# Revit family: Indoor_Floor Lamp_Santa&Cole_Diana-Diana Mayor
name_source: partatom
category: Luminarias
revit_build: Autodesk Revit 2018 (Build: 20190510_1515(x64)
units: mm (PartAtom-declared; Revit-internal decimal feet)

## family parameters
Compartido = No
Corte con vacíos al cargar = No
Cota de conector redondo = Diámetro de uso
Número OmniClass = 23.80.70.00
Origen de luz = Sí
Punto de cálculo de habitación = No
Se basa en plano de trabajo = No
Siempre vertical = Sí
Tipo de pieza = Normal
Título OmniClass = Lighting

## types (8) — shared parameters
Assembly instructions - CE = https://www.santacole.com
Assembly instructions - UL = https://www.santacole.com
Cambio de temperatura de color de luz atenuada = <Ninguno>
Carga aparente = 12 VA
Energy Label = https://www.santacole.com
Fabricante = Santa & Cole
Filtro de color = 16777215
Load = 12 W
Manufacturer website = http://www.santacole.com
Modelo = Diana
Second Bulb = Bulb : 1521 lm
Tamaño de símbolo de origen de luz = 50 mm  [stored 0.164042 ft]
Technical Information = https://www.santacole.com
URL = https://www.santacole.com

## per-type parameters (varying)
| type | Code | Lampshade Material | Light Source Elevation | Structure Material | Visibility_Diana | Visibility_Diana Mayor |
| Diana - Black Linen Lampshade with Brass Structure | DIA31/DIA313+DIAGx | Santa & Cole - Black Linen | 1264 mm | Santa & Cole - Brass | Sí | No |
| Diana - Black Linen Lampshade with Nickel Structure | DIA21/DIA213+DIAMx | Santa & Cole - Black Linen | 1264 mm | Santa & Cole - Nickel | Sí | No |
| Diana - White Linen Lampshade with Nickel Structure | DIA21/DIA213+DIAMx | Santa & Cole - White Linen | 1264 mm | Santa & Cole - Nickel | Sí | No |
| Diana - White Linen Lampshade with Brass Structure | DIA21/DIA213+DIAMx | Santa & Cole - White Linen | 1264 mm | Santa & Cole - Brass | Sí | No |
| Diana Mayor - White Linen Lampshade with Brass Structure | DIA31/DIA313+DIAGx | Santa & Cole - White Linen | 1552 mm  [stored 5.09186 ft] | Santa & Cole - Brass | No | Sí |
| Diana Mayor - White Linen Lampshade with Nickel Structure | DIA31/DIA313+DIAGx | Santa & Cole - White Linen | 1552 mm  [stored 5.09186 ft] | Santa & Cole - Nickel | No | Sí |
| Diana Mayor - Black Linen Lampshade with Brass Structure | DIA31/DIA313+DIAGx | Santa & Cole - Black Linen | 1552 mm  [stored 5.09186 ft] | Santa & Cole - Brass | No | Sí |
| Diana Mayor - Black Linen Lampshade with Nickel Structure | DIA31/DIA313+DIAGx | Santa & Cole - Black Linen | 1552 mm  [stored 5.09186 ft] | Santa & Cole - Nickel | No | Sí |

note: [stored X ft] marks values corroborated as IEEE doubles in the binary element streams (Revit-internal decimal feet)

## geometry (parser evidence)
native form markers: Sweep x6
no freeform markers — native parametric forms only
